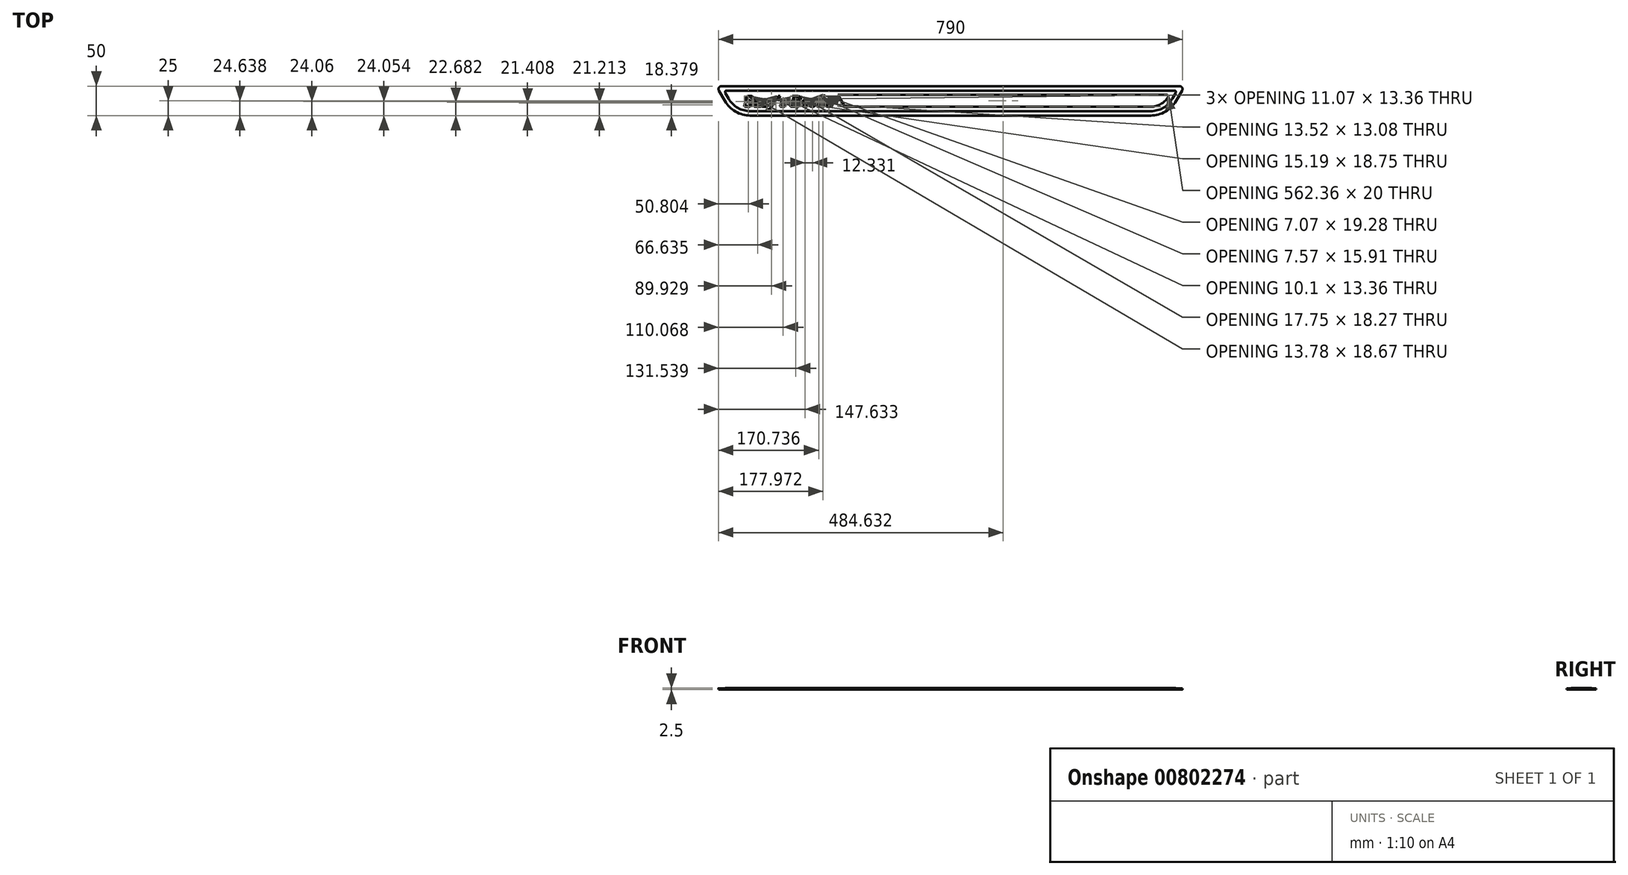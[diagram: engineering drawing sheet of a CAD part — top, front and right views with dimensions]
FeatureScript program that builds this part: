
annotation { "Feature Type Name" : "Feature", "Feature Type Description" : "" }
export const myFeature = defineFeature(function(context is Context, id is Id, definition is map)
    precondition{}
    {
        {
            var Q0;
            Q0=qCreatedBy(makeId("Top.planeOp"),FACE);
            var sketch = newSketch(context, id + "F0", { "sketchPlane" : qUnion([Q0])});
            skLineSegment(sketch, "E0.bottom", {"start": v(340.93, -25) * mm, "end": v(-340.93, -25) * mm});
            skLineSegment(sketch, "E0.top", {"start": v(390, 25) * mm, "end": v(-390, 25) * mm});
            skPoint(sketch, "E0.middle", {"position": v(0, 0) * mm});
            skLineSegment(sketch, "E1", {"start": v(-394.33, 17.5) * mm, "end": v(-384.23, 0) * mm});
            skLineSegment(sketch, "E2", {"start": v(394.33, 17.5) * mm, "end": v(384.23, 0) * mm});
            skPoint(sketch, "E3.orphan", {"position": v(-398.66, -25) * mm});
            skPoint(sketch, "E0.left.start.orphan", {"position": v(398.66, -25) * mm});
            skPoint(sketch, "E4.visualSharp", {"position": v(398.66, 25) * mm});
            skArc(sketch, "E4.filletArc", {"start": v(394.33, 17.5) * mm, "mid": v(394.33, 22.5) * mm, "end": v(390, 25) * mm});
            skPoint(sketch, "E5.visualSharp", {"position": v(-398.66, 25) * mm});
            skArc(sketch, "E5.filletArc", {"start": v(-390, 25) * mm, "mid": v(-394.33, 22.5) * mm, "end": v(-394.33, 17.5) * mm});
            skPoint(sketch, "E6.visualSharp", {"position": v(-369.8, -25) * mm});
            skArc(sketch, "E6.filletArc", {"start": v(-384.23, 0) * mm, "mid": v(-365.93, -18.3) * mm, "end": v(-340.93, -25) * mm});
            skPoint(sketch, "E7.visualSharp", {"position": v(369.8, -25) * mm});
            skArc(sketch, "E7.filletArc", {"start": v(340.93, -25) * mm, "mid": v(365.93, -18.3) * mm, "end": v(384.23, 0) * mm});
            skSolve(sketch);
        }
        {
            var Q0;
            Q0=makeQuery(id+"F0.imprint","IMPRINT",FACE,{"disambiguationData":[TD([[makeQuery(id+"F0.imprint","IMPRINT",EDGE,{"derivedFrom":sQuery(id+"F0.wireOp",EDGE,"E0.bottom")}),-1.0]])]});
            extrude(context, id + "F1", {"entities" : qUnion([Q0]), "depth" : 2 * mm, "offsetDistance" : 25 * mm});
        }
        {
            var Q0;
            Q0=makeQuery(id+"F1.opExtrude","CAP_FACE",FACE,{"disambiguationData":[OSD([sQuery(id+"F0.wireOp",EDGE,"E0.bottom"),sQuery(id+"F0.wireOp",EDGE,"E0.top"),sQuery(id+"F0.wireOp",EDGE,"E1"),sQuery(id+"F0.wireOp",EDGE,"E2"),sQuery(id+"F0.wireOp",EDGE,"E4.filletArc"),sQuery(id+"F0.wireOp",EDGE,"E5.filletArc"),sQuery(id+"F0.wireOp",EDGE,"E6.filletArc"),sQuery(id+"F0.wireOp",EDGE,"E7.filletArc")])],"isStart":false});
            var sketch = newSketch(context, id + "F2", { "sketchPlane" : qUnion([Q0])});
            skLineSegment(sketch, "E8.0", {"start": v(377.73, 3.75) * mm, "end": v(383.5, 13.75) * mm});
            skLineSegment(sketch, "E8.1", {"start": v(-383.5, 13.75) * mm, "end": v(-377.73, 3.75) * mm});
            skArc(sketch, "E8.2", {"start": v(-377.73, 3.75) * mm, "mid": v(-362.18, -11.8) * mm, "end": v(-340.93, -17.5) * mm});
            skLineSegment(sketch, "E8.3", {"start": v(381.34, 17.5) * mm, "end": v(-381.34, 17.5) * mm});
            skLineSegment(sketch, "E8.4", {"start": v(-340.93, -17.5) * mm, "end": v(340.93, -17.5) * mm});
            skArc(sketch, "E8.5", {"start": v(340.93, -17.5) * mm, "mid": v(362.18, -11.8) * mm, "end": v(377.73, 3.75) * mm});
            skPoint(sketch, "E9.visualSharp", {"position": v(-385.67, 17.5) * mm});
            skArc(sketch, "E9.filletArc", {"start": v(-381.34, 17.5) * mm, "mid": v(-383.5, 16.25) * mm, "end": v(-383.5, 13.75) * mm});
            skPoint(sketch, "E10.visualSharp", {"position": v(385.67, 17.5) * mm});
            skArc(sketch, "E10.filletArc", {"start": v(383.5, 13.75) * mm, "mid": v(383.5, 16.25) * mm, "end": v(381.34, 17.5) * mm});
            skLineSegment(sketch, "E11.0", {"start": v(368.31, 10) * mm, "end": v(-191.55, 10) * mm});
            skArc(sketch, "E11.1", {"start": v(340.93, -10) * mm, "mid": v(357.74, -5.7) * mm, "end": v(370.42, 6.15) * mm});
            skLineSegment(sketch, "E11.2", {"start": v(-180, -10) * mm, "end": v(340.93, -10) * mm});
            skLineSegment(sketch, "E12", {"start": v(-191.55, 10) * mm, "end": v(-180, -10) * mm});
            skPoint(sketch, "E13.0.2.start.orphan", {"position": v(-390, 25) * mm});
            skPoint(sketch, "E13.0.3.start.orphan", {"position": v(-394.33, 17.5) * mm});
            skPoint(sketch, "E13.0.4.start.orphan", {"position": v(-384.23, 0) * mm});
            skPoint(sketch, "E13.0.5.start.orphan", {"position": v(-340.93, -25) * mm});
            skPoint(sketch, "E13.0.0.end.orphan", {"position": v(390, 25) * mm});
            skPoint(sketch, "E13.0.7.end.orphan", {"position": v(394.33, 17.5) * mm});
            skPoint(sketch, "E13.0.6.end.orphan", {"position": v(384.23, 0) * mm});
            skPoint(sketch, "E13.0.6.start.orphan", {"position": v(340.93, -25) * mm});
            skPoint(sketch, "E14.visualSharp", {"position": v(372.55, 10) * mm});
            skArc(sketch, "E14.filletArc", {"start": v(370.42, 6.15) * mm, "mid": v(370.5, 8.7) * mm, "end": v(368.31, 10) * mm});
            skSolve(sketch);
        }
        {
            var Q0;
            Q0=qSketchRegion(id+"F2",true);
            extrude(context, id + "F3", {"entities" : qUnion([Q0]), "depth" : .5 * mm, "offsetDistance" : 25 * mm});
        }
        {
            var Q0;
            Q0=makeQuery(id+"F3.opExtrude","CAP_FACE",FACE,{"disambiguationData":[OSD([sQuery(id+"F2.wireOp",EDGE,"E8.0"),sQuery(id+"F2.wireOp",EDGE,"E8.1"),sQuery(id+"F2.wireOp",EDGE,"E8.2"),sQuery(id+"F2.wireOp",EDGE,"E8.3"),sQuery(id+"F2.wireOp",EDGE,"E8.4"),sQuery(id+"F2.wireOp",EDGE,"E8.5"),sQuery(id+"F2.wireOp",EDGE,"E9.filletArc"),sQuery(id+"F2.wireOp",EDGE,"E10.filletArc"),sQuery(id+"F2.wireOp",EDGE,"E11.0"),sQuery(id+"F2.wireOp",EDGE,"E11.1"),sQuery(id+"F2.wireOp",EDGE,"E11.2"),sQuery(id+"F2.wireOp",EDGE,"E12"),sQuery(id+"F2.wireOp",EDGE,"E14.filletArc")])],"isStart":false});
            var sketch = newSketch(context, id + "F4", { "sketchPlane" : qUnion([Q0])});
            skText(sketch, "E15", { "text": "Suzy\'s Beetle", "fontName": "Tinos-BoldItalic.ttf"});
            skLineSegment(sketch, "E16", {"start": v(-185.77, 0) * mm, "end": v(-94.05, 0) * mm, "construction": true});
            const initialGuessF4  = {"E15": [-0.35159, -0.01, 1, 0, 0.02]};
            skSetInitialGuess(sketch, initialGuessF4);
            skSolve(sketch);
        }
        {
            var Q0;
            Q0=qSketchRegion(id+"F4",true);
            extrude(context, id + "F5", {"entities" : qUnion([Q0]), "operationType" : NewBodyOperationType.REMOVE, "oppositeDirection" : true, "depth" : .5 * mm, "offsetDistance" : 25 * mm});
        }
    });
